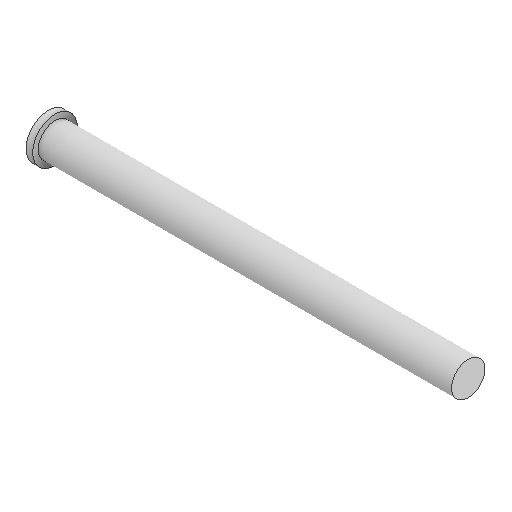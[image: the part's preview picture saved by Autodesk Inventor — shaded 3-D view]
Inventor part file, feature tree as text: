
AUTODESK INVENTOR PART (.ipt)
format: ipt  version: 2022 (Build 260153000, 153)  size: 86,528 bytes
history: native  units: in
note: dims shown in document units (in); Inventor stores cm internally (conversion verified against a paired STEP export)
features: extrude x1
ambient origin geometry x8: Origin, YZ Plane, XZ Plane, XY Plane, X Axis, Y Axis, Z Axis, Center Point
bodies: Solid1 (feature_tree)
feature tree (1):
  extrude  "Extrude2"  [1 undecoded]
note: 1 required parameter value undecoded (feature->parameter linkage not recoverable at this tier; creation-order binding heuristic only, values carry confidence <= 0.55)
